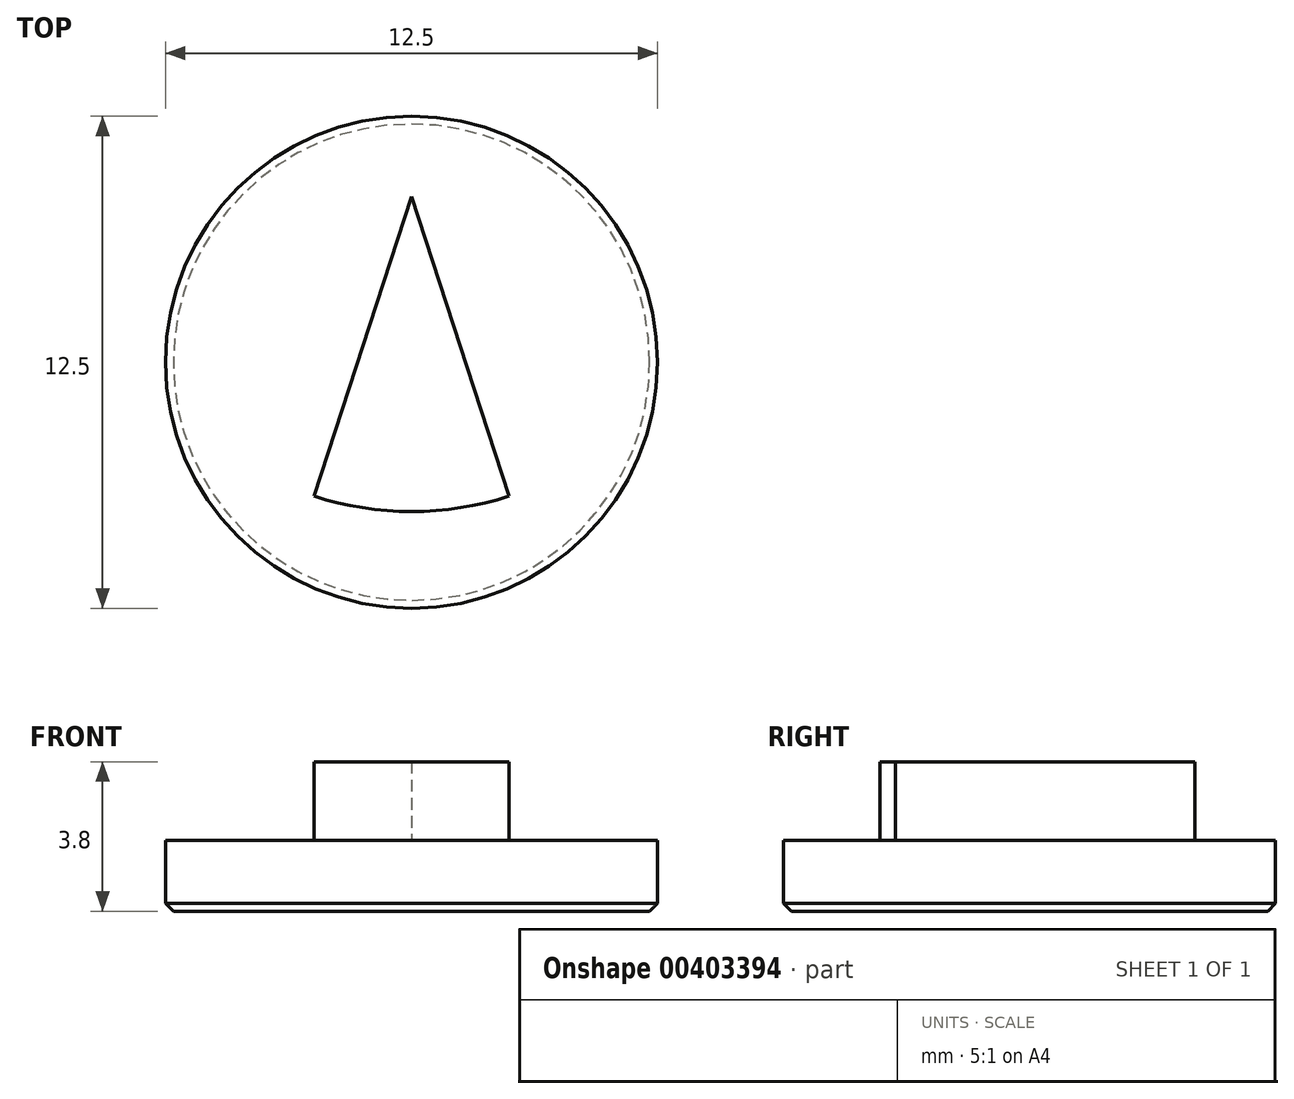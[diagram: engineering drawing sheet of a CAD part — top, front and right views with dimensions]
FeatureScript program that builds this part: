
annotation { "Feature Type Name" : "Feature", "Feature Type Description" : "" }
export const myFeature = defineFeature(function(context is Context, id is Id, definition is map)
    precondition{}
    {
        {
            var Q0;
            Q0=qCreatedBy(makeId("Top.planeOp"),FACE);
            var sketch = newSketch(context, id + "F0", { "sketchPlane" : qUnion([Q0])});
            skCircle(sketch, "E0", {"center": v(0, 0) * mm, "radius": 6.25 * mm});
            skSolve(sketch);
        }
        {
            var Q0;
            Q0=makeQuery(id+"F0.imprint","IMPRINT",FACE,{"disambiguationData":[TD([[makeQuery(id+"F0.imprint","IMPRINT",EDGE,{"derivedFrom":sQuery(id+"F0.wireOp",EDGE,"E0")}),1.0]])]});
            extrude(context, id + "F1", {"entities" : qUnion([Q0]), "depth" : 1.8 * mm});
        }
        {
            var Q0;
            Q0=makeQuery(id+"F1.opExtrude","CAP_FACE",FACE,{"disambiguationData":[OSD([sQuery(id+"F0.wireOp",EDGE,"E0")])],"isStart":false});
            var sketch = newSketch(context, id + "F2", { "sketchPlane" : qUnion([Q0])});
            skCircle(sketch, "E1.cCircle", {"center": v(0, 0) * mm, "radius": 4.2 * mm, "construction": true});
            skLineSegment(sketch, "E1.0", {"start": v(0, 4.2) * mm, "end": v(4, 1.3) * mm, "construction": true});
            skLineSegment(sketch, "E1.1", {"start": v(4, 1.3) * mm, "end": v(2.47, -3.4) * mm, "construction": true});
            skLineSegment(sketch, "E1.2", {"start": v(2.47, -3.4) * mm, "end": v(-2.47, -3.4) * mm, "construction": true});
            skLineSegment(sketch, "E1.3", {"start": v(-2.47, -3.4) * mm, "end": v(-4, 1.3) * mm, "construction": true});
            skLineSegment(sketch, "E1.4", {"start": v(-4, 1.3) * mm, "end": v(0, 4.2) * mm, "construction": true});
            skLineSegment(sketch, "E2", {"start": v(0, 4.2) * mm, "end": v(-2.47, -3.4) * mm});
            skLineSegment(sketch, "E3", {"start": v(0, 4.2) * mm, "end": v(2.47, -3.4) * mm});
            skArc(sketch, "E4", {"start": v(-2.47, -3.4) * mm, "mid": v(0, -3.8) * mm, "end": v(2.47, -3.4) * mm});
            skSolve(sketch);
        }
        {
            var Q0;
            Q0 = qSketchRegion(id + "F2", true);
            extrude(context, id + "F3", {"entities" : qUnion([Q0]), "operationType" : NewBodyOperationType.ADD, "depth" : 2 * mm});
        }
        {
            var Q0;
            Q0=makeQuery(id+"F1.opExtrude","CAP_FACE",FACE,{"disambiguationData":[OSD([sQuery(id+"F0.wireOp",EDGE,"E0")])],"isStart":true});
            chamfer(context, id + "F4", {"entities" : qUnion([Q0]), "width" : 0.2 * mm});
        }
    });
